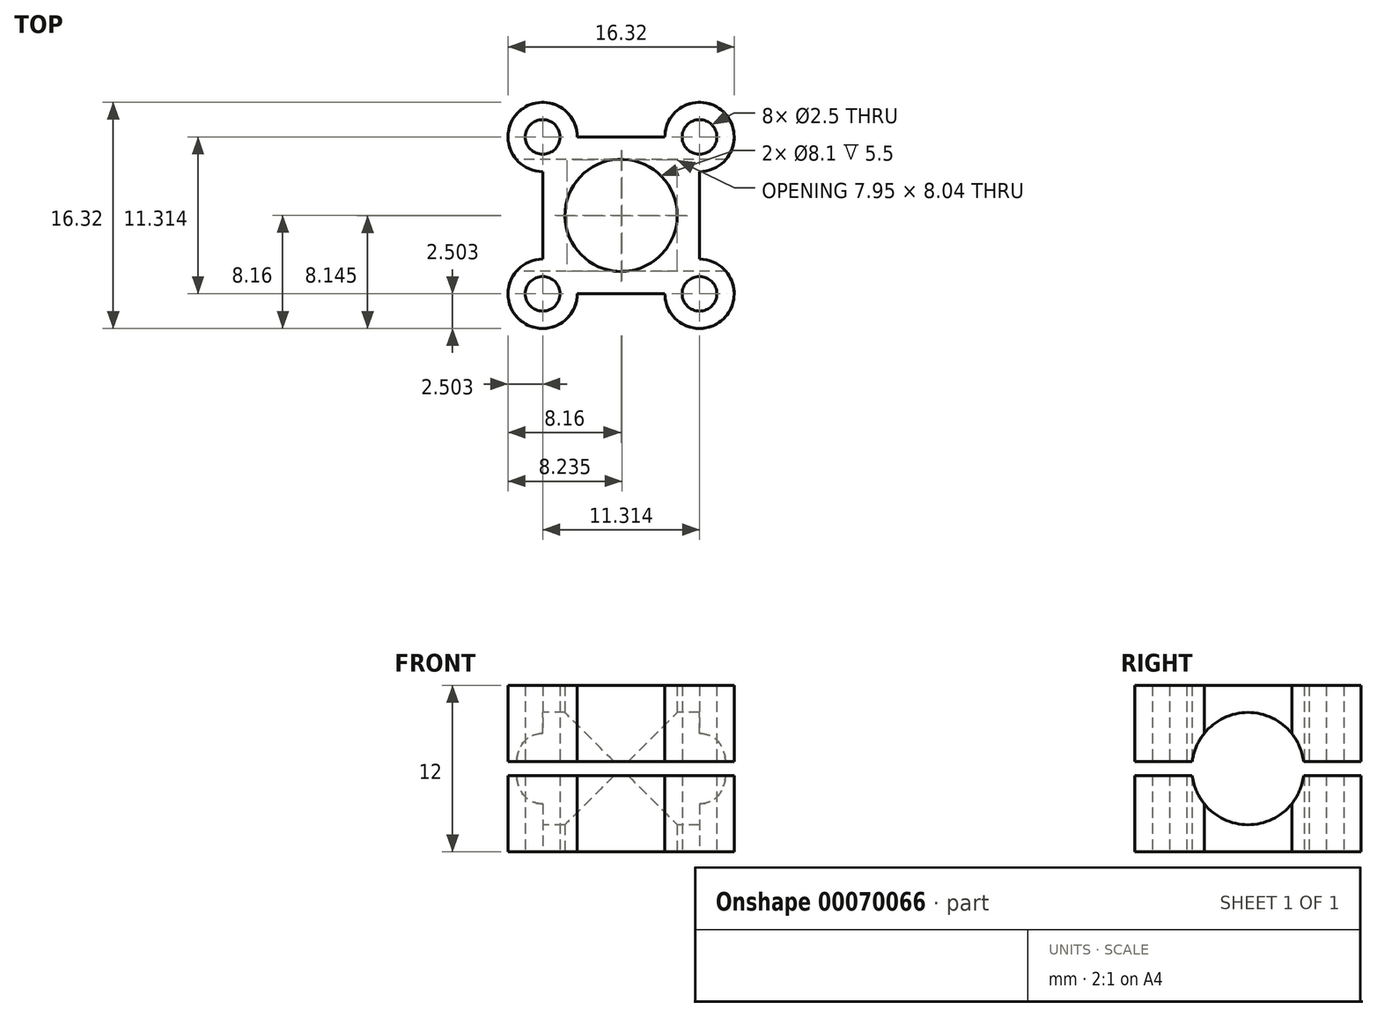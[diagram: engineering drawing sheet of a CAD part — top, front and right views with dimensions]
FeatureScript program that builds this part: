
annotation { "Feature Type Name" : "Feature", "Feature Type Description" : "" }
export const myFeature = defineFeature(function(context is Context, id is Id, definition is map)
    precondition{}
    {
        {
            var Q0;
            Q0=qCreatedBy(makeId("Top.planeOp"),FACE);
            var sketch = newSketch(context, id + "F0", { "sketchPlane" : qUnion([Q0])});
            skPoint(sketch, "E0.0", {"position": v(0, 0) * mm});
            skLineSegment(sketch, "E1.rect.bottom", {"start": v(5.66, 5.66) * mm, "end": v(-5.66, 5.66) * mm, "construction": true});
            skLineSegment(sketch, "E1.rect.top", {"start": v(5.66, -5.66) * mm, "end": v(-5.66, -5.66) * mm, "construction": true});
            skLineSegment(sketch, "E1.rect.left", {"start": v(5.66, 5.66) * mm, "end": v(5.66, -5.66) * mm, "construction": true});
            skLineSegment(sketch, "E1.rect.right", {"start": v(-5.66, 5.66) * mm, "end": v(-5.66, -5.66) * mm, "construction": true});
            skLineSegment(sketch, "E2", {"start": v(-5.66, -5.66) * mm, "end": v(5.66, 5.66) * mm, "construction": true});
            skLineSegment(sketch, "E3", {"start": v(-5.66, 5.66) * mm, "end": v(5.66, -5.66) * mm, "construction": true});
            skCircle(sketch, "E4", {"center": v(-5.66, 5.66) * mm, "radius": 1.25 * mm});
            skCircle(sketch, "E5", {"center": v(5.66, 5.66) * mm, "radius": 1.25 * mm});
            skCircle(sketch, "E6", {"center": v(-5.66, -5.66) * mm, "radius": 1.25 * mm});
            skCircle(sketch, "E7", {"center": v(5.66, -5.66) * mm, "radius": 1.25 * mm});
            skCircle(sketch, "E8", {"center": v(-5.66, 5.66) * mm, "radius": 2.5 * mm});
            skCircle(sketch, "E9", {"center": v(5.66, 5.66) * mm, "radius": 2.5 * mm});
            skCircle(sketch, "E10", {"center": v(-5.66, -5.66) * mm, "radius": 2.5 * mm});
            skCircle(sketch, "E11", {"center": v(5.66, -5.66) * mm, "radius": 2.5 * mm});
            skLineSegment(sketch, "E12", {"start": v(-5.66, 3.16) * mm, "end": v(-5.66, -3.16) * mm});
            skLineSegment(sketch, "E13", {"start": v(-3.16, -5.66) * mm, "end": v(3.16, -5.66) * mm});
            skLineSegment(sketch, "E14", {"start": v(5.66, 3.16) * mm, "end": v(5.66, -3.16) * mm});
            skLineSegment(sketch, "E15", {"start": v(-3.16, 5.66) * mm, "end": v(3.16, 5.66) * mm});
            skCircle(sketch, "E16", {"center": v(0, 0) * mm, "radius": 4.05 * mm});
            skSolve(sketch);
        }
        {
            var Q0;
            Q0 = qSketchRegion(id + "F0", true);
            extrude(context, id + "F1", {"entities" : qUnion([Q0]), "endBound" : BoundingType.SYMMETRIC, "depth" : 12 * mm});
        }
        {
            var Q0;
            Q0=qCreatedBy(makeId("Right.planeOp"),FACE);
            var sketch = newSketch(context, id + "F2", { "sketchPlane" : qUnion([Q0])});
            skCircle(sketch, "E17", {"center": v(0, 0) * mm, "radius": 4.05 * mm});
            skSolve(sketch);
        }
        {
            var Q0;
            Q0 = qSketchRegion(id + "F2", true);
            extrude(context, id + "F3", {"entities" : qUnion([Q0]), "operationType" : NewBodyOperationType.REMOVE, "endBound" : BoundingType.THROUGH_ALL, "depth" : 25 * mm, "hasSecondDirection" : true, "secondDirectionBound" : SecondDirectionBoundingType.THROUGH_ALL, "secondDirectionOppositeDirection" : true, "secondDirectionDepth" : 25 * mm});
        }
        {
            var Q0;
            Q0=qCreatedBy(makeId("Top.planeOp"),FACE);
            var sketch = newSketch(context, id + "F4", { "sketchPlane" : qUnion([Q0])});
            skLineSegment(sketch, "E18.rect.bottom", {"start": v(13.6, 12) * mm, "end": v(-13.6, 12) * mm});
            skLineSegment(sketch, "E18.rect.top", {"start": v(13.6, -12) * mm, "end": v(-13.6, -12) * mm});
            skLineSegment(sketch, "E18.rect.left", {"start": v(13.6, 12) * mm, "end": v(13.6, -12) * mm});
            skLineSegment(sketch, "E18.rect.right", {"start": v(-13.6, 12) * mm, "end": v(-13.6, -12) * mm});
            skPoint(sketch, "E18.rect.middle", {"position": v(0, 0) * mm});
            skSolve(sketch);
        }
        {
            var Q0;
            Q0 = qSketchRegion(id + "F4", true);
            extrude(context, id + "F5", {"entities" : qUnion([Q0]), "operationType" : NewBodyOperationType.REMOVE, "endBound" : BoundingType.SYMMETRIC, "oppositeDirection" : true, "depth" : 1 * mm});
        }
    });
